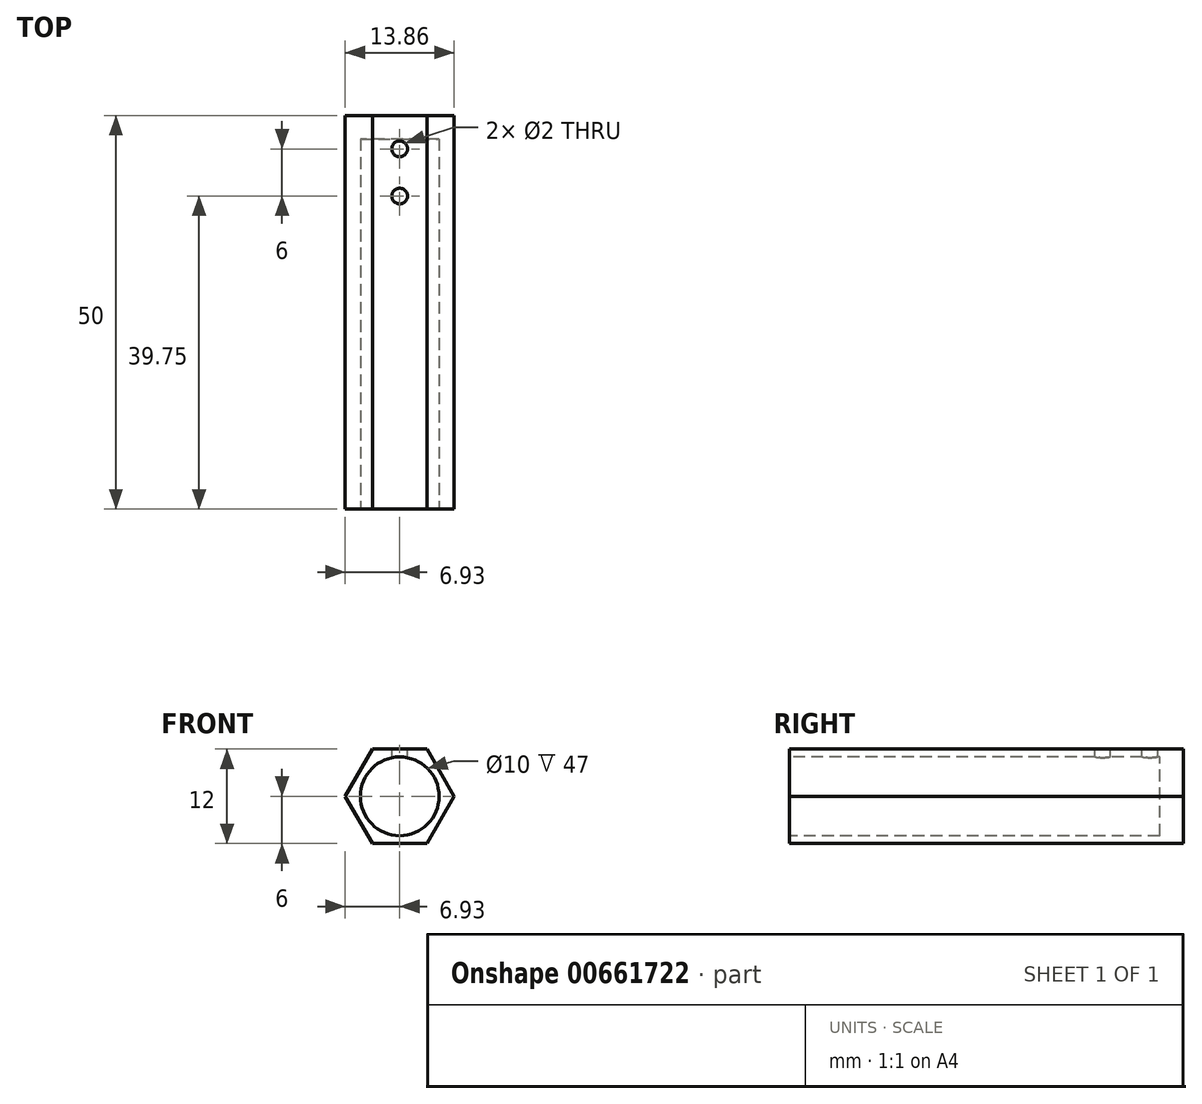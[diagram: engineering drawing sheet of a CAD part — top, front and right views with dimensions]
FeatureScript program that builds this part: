
annotation { "Feature Type Name" : "Feature", "Feature Type Description" : "" }
export const myFeature = defineFeature(function(context is Context, id is Id, definition is map)
    precondition{}
    {
        {
            var Q0;
            Q0=qCreatedBy(makeId("Front.planeOp"),FACE);
            var sketch = newSketch(context, id + "F0", { "sketchPlane" : qUnion([Q0])});
            skCircle(sketch, "E0.cCircle", {"center": v(0, 0) * mm, "radius": 6 * mm, "construction": true});
            skLineSegment(sketch, "E0.0", {"start": v(-3.46, 6) * mm, "end": v(3.46, 6) * mm});
            skLineSegment(sketch, "E0.1", {"start": v(3.46, 6) * mm, "end": v(6.93, 0) * mm});
            skLineSegment(sketch, "E0.2", {"start": v(6.93, 0) * mm, "end": v(3.46, -6) * mm});
            skLineSegment(sketch, "E0.3", {"start": v(3.46, -6) * mm, "end": v(-3.46, -6) * mm});
            skLineSegment(sketch, "E0.4", {"start": v(-3.46, -6) * mm, "end": v(-6.93, 0) * mm});
            skLineSegment(sketch, "E0.5", {"start": v(-6.93, 0) * mm, "end": v(-3.46, 6) * mm});
            skPoint(sketch, "E0.0.midPoint", {"position": v(0, 6) * mm});
            skSolve(sketch);
        }
        {
            var Q0;
            Q0=makeQuery(id+"F0.imprint","IMPRINT",FACE,{"disambiguationData":[TD([[makeQuery(id+"F0.imprint","IMPRINT",EDGE,{"derivedFrom":sQuery(id+"F0.wireOp",EDGE,"E0.0")}),-1.0]])]});
            extrude(context, id + "F1", {"entities" : qUnion([Q0]), "depth" : 50 * mm, "offsetDistance" : 25 * mm});
        }
        {
            var Q0;
            Q0=makeQuery(id+"F1.opExtrude","CAP_FACE",FACE,{"disambiguationData":[OSD([sQuery(id+"F0.wireOp",EDGE,"E0.0"),sQuery(id+"F0.wireOp",EDGE,"E0.1"),sQuery(id+"F0.wireOp",EDGE,"E0.2"),sQuery(id+"F0.wireOp",EDGE,"E0.3"),sQuery(id+"F0.wireOp",EDGE,"E0.4"),sQuery(id+"F0.wireOp",EDGE,"E0.5")])],"isStart":false});
            var sketch = newSketch(context, id + "F2", { "sketchPlane" : qUnion([Q0])});
            skCircle(sketch, "E1", {"center": v(0, 0) * mm, "radius": 5 * mm});
            skSolve(sketch);
        }
        {
            var Q0;
            Q0=makeQuery(id+"F2.imprint","IMPRINT",FACE,{"disambiguationData":[TD([[makeQuery(id+"F2.imprint","IMPRINT",EDGE,{"derivedFrom":sQuery(id+"F2.wireOp",EDGE,"E1")}),1.0]])]});
            extrude(context, id + "F3", {"entities" : qUnion([Q0]), "operationType" : NewBodyOperationType.REMOVE, "oppositeDirection" : true, "depth" : 47 * mm, "offsetDistance" : 25 * mm});
        }
        {
            var Q0;
            Q0=makeQuery(id+"F1.opExtrude","SWEPT_FACE",FACE,{"disambiguationData":[OSD([sQuery(id+"F0.wireOp",EDGE,"E0.0")])]});
            var sketch = newSketch(context, id + "F4", { "sketchPlane" : qUnion([Q0])});
            skCircle(sketch, "E2", {"center": v(0, -4.25) * mm, "radius": 1 * mm});
            skCircle(sketch, "E3", {"center": v(0, -10.25) * mm, "radius": 1 * mm});
            skSolve(sketch);
        }
        {
            var Q0;
            Q0=makeQuery(id+"F4.imprint","IMPRINT",FACE,{"disambiguationData":[TD([[makeQuery(id+"F4.imprint","IMPRINT",EDGE,{"derivedFrom":sQuery(id+"F4.wireOp",EDGE,"E3")}),1.0]])]});
            var Q1;
            Q1=makeQuery(id+"F4.imprint","IMPRINT",FACE,{"disambiguationData":[TD([[makeQuery(id+"F4.imprint","IMPRINT",EDGE,{"derivedFrom":sQuery(id+"F4.wireOp",EDGE,"E2")}),1.0]])]});
            extrude(context, id + "F5", {"entities" : qUnion([Q0, Q1]), "operationType" : NewBodyOperationType.REMOVE, "oppositeDirection" : true, "depth" : 2 * mm, "offsetDistance" : 25 * mm});
        }
    });
